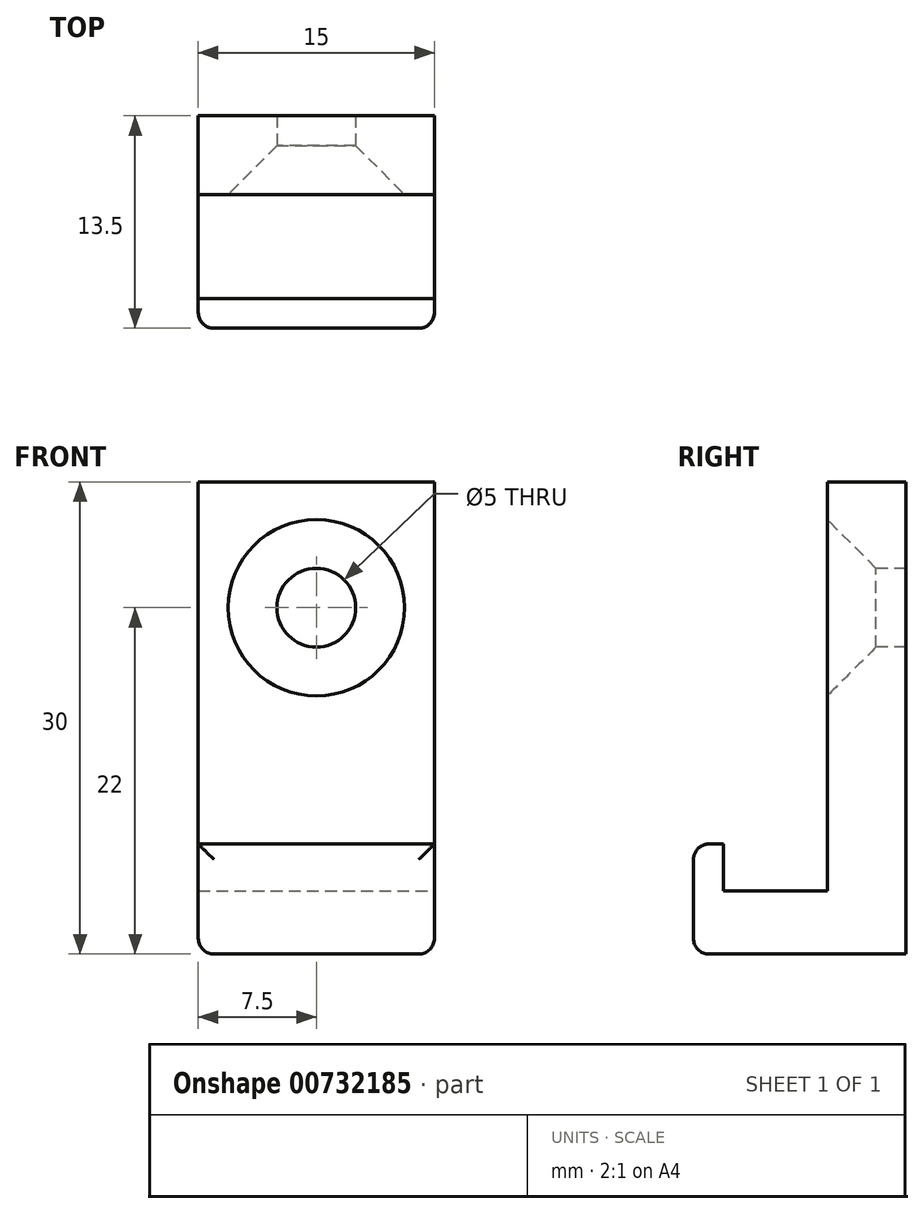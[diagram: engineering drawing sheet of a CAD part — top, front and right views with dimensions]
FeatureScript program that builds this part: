
annotation { "Feature Type Name" : "Feature", "Feature Type Description" : "" }
export const myFeature = defineFeature(function(context is Context, id is Id, definition is map)
    precondition{}
    {
        {
            var Q0;
            Q0=qCreatedBy(makeId("Front.planeOp"),FACE);
            var sketch = newSketch(context, id + "F0", { "sketchPlane" : qUnion([Q0])});
            skLineSegment(sketch, "E0.bottom", {"start": v(-7.5, 15) * mm, "end": v(7.5, 15) * mm});
            skLineSegment(sketch, "E0.top", {"start": v(-7.5, -15) * mm, "end": v(7.5, -15) * mm});
            skLineSegment(sketch, "E0.left", {"start": v(-7.5, 15) * mm, "end": v(-7.5, -15) * mm});
            skLineSegment(sketch, "E0.right", {"start": v(7.5, 15) * mm, "end": v(7.5, -15) * mm});
            skLineSegment(sketch, "E1", {"start": v(-55.38, 0) * mm, "end": v(56.17, 0) * mm, "construction": true});
            skLineSegment(sketch, "E2", {"start": v(0, 15) * mm, "end": v(0, -3.56) * mm, "construction": true});
            skLineSegment(sketch, "E3", {"start": v(-31.34, 0) * mm, "end": v(7.5, 0) * mm, "construction": true});
            skSolve(sketch);
        }
        {
            var Q0;
            Q0=makeQuery(id+"F0.imprint","IMPRINT",FACE,{"disambiguationData":[TD([[makeQuery(id+"F0.imprint","IMPRINT",EDGE,{"derivedFrom":sQuery(id+"F0.wireOp",EDGE,"E0.bottom")}),-1.0]])]});
            extrude(context, id + "F1", {"entities" : qUnion([Q0]), "depth" : 5 * mm, "offsetDistance" : 25 * mm});
        }
        {
            var Q0;
            Q0=makeQuery(id+"F1.opExtrude","CAP_FACE",FACE,{"disambiguationData":[OSD([sQuery(id+"F0.wireOp",EDGE,"E0.bottom"),sQuery(id+"F0.wireOp",EDGE,"E0.top"),sQuery(id+"F0.wireOp",EDGE,"E0.left"),sQuery(id+"F0.wireOp",EDGE,"E0.right")])],"isStart":false});
            var sketch = newSketch(context, id + "F2", { "sketchPlane" : qUnion([Q0])});
            skLineSegment(sketch, "E4", {"start": v(-15.15, 0) * mm, "end": v(12.94, 0) * mm, "construction": true});
            skLineSegment(sketch, "E5", {"start": v(0, -6.11) * mm, "end": v(0, 4.39) * mm, "construction": true});
            skPoint(sketch, "E6", {"position": v(0, 7) * mm});
            skSolve(sketch);
        }
        {
            var Q0;
            Q0=sQuery(id+"F2.wireOp",VERTEX,"E6");
            var Q1;
            Q1=makeQuery(id+"F1.opExtrude","SWEPT_BODY",BODY,{"disambiguationData":[OSD([sQuery(id+"F0.wireOp",EDGE,"E0.bottom"),sQuery(id+"F0.wireOp",EDGE,"E0.top"),sQuery(id+"F0.wireOp",EDGE,"E0.left"),sQuery(id+"F0.wireOp",EDGE,"E0.right")])]});
            hole(context, id + "F3", {"style" : HoleStyle.C_SINK, "endStyle" : HoleEndStyle.THROUGH, "standardTappedOrClearance" : lookupTablePath({ "standard" : "ISO", "size" : "5", "type" : "Drilled" }), "standardBlindInLast" : lookupTablePath({ "standard" : "ISO", "size" : "5", "type" : "Drilled" }), "holeDiameter" : 5 * mm, "cSinkDiameter" : 11.2 * mm, "cSinkAngle" : 90 * degree, "majorDiameter" : 5 * mm, "isTappedThrough" : true, "tappedDepth" : 12 * mm, "tapClearance" : 3, "locations" : qUnion([Q0]), "scope" : qUnion([Q1])});
        }
        {
            var Q0;
            Q0=makeQuery(id+"F1.opExtrude","CAP_FACE",FACE,{"disambiguationData":[OSD([sQuery(id+"F0.wireOp",EDGE,"E0.bottom"),sQuery(id+"F0.wireOp",EDGE,"E0.top"),sQuery(id+"F0.wireOp",EDGE,"E0.left"),sQuery(id+"F0.wireOp",EDGE,"E0.right")])],"isStart":false});
            var sketch = newSketch(context, id + "F4", { "sketchPlane" : qUnion([Q0])});
            skLineSegment(sketch, "E7", {"start": v(-7.5, -11) * mm, "end": v(7.5, -11) * mm});
            skLineSegment(sketch, "E8", {"start": v(7.5, -11) * mm, "end": v(7.5, -15) * mm});
            skLineSegment(sketch, "E9", {"start": v(7.5, -15) * mm, "end": v(-7.5, -15) * mm});
            skLineSegment(sketch, "E10", {"start": v(-7.5, -15) * mm, "end": v(-7.5, -11) * mm});
            skSolve(sketch);
        }
        {
            var Q0;
            Q0=makeQuery(id+"F4.imprint","IMPRINT",FACE,{"disambiguationData":[TD([[makeQuery(id+"F4.imprint","IMPRINT",EDGE,{"derivedFrom":sQuery(id+"F4.wireOp",EDGE,"E7")}),-1.0]])]});
            extrude(context, id + "F5", {"entities" : qUnion([Q0]), "operationType" : NewBodyOperationType.ADD, "depth" : 8.5 * mm, "offsetDistance" : 25 * mm});
        }
        {
            var Q0;
            Q0=makeQuery(id+"F5.opExtrude","SWEPT_FACE",FACE,{"disambiguationData":[OSD([sQuery(id+"F4.wireOp",EDGE,"E7")])]});
            var sketch = newSketch(context, id + "F6", { "sketchPlane" : qUnion([Q0])});
            skLineSegment(sketch, "E11", {"start": v(-7.5, -11.6) * mm, "end": v(7.5, -11.6) * mm});
            skSolve(sketch);
        }
        {
            var Q0;
            {var subQ0=sQuery(id+"F6.wireOp",EDGE,"E11");Q0=makeQuery(id+"F6.imprint","IMPRINT",FACE,{"disambiguationData":[TD([[makeQuery(id+"F6.imprint","IMPRINT",EDGE,{"derivedFrom":subQ0}),-1.0]])]});}
            extrude(context, id + "F7", {"entities" : qUnion([Q0]), "operationType" : NewBodyOperationType.ADD, "depth" : 3 * mm, "offsetDistance" : 25 * mm});
        }
        {
            var Q0;
            Q0=makeQuery(id+"F7.opExtrude","CAP_EDGE",EDGE,{"disambiguationData":[OSD([sQuery(id+"F4.wireOp",EDGE,"E7")])],"isStart":false});
            var Q1;
            {var subQ0=sQuery(id+"F4.wireOp",EDGE,"E8");Q1=makeQuery(id+"F7.boolean.opBoolean","MERGE",EDGE,{"derivedFrom":[makeQuery(id+"F5.opExtrude","CAP_EDGE",EDGE,{"disambiguationData":[OSD([subQ0])],"isStart":false}),makeQuery(id+"F7.opExtrude","SWEPT_EDGE",EDGE,{"disambiguationData":[OSD([sQuery(id+"F0.wireOp",EDGE,"E0.right"),sQuery(id+"F4.wireOp",EDGE,"E7"),subQ0])]})]});}
            var Q2;
            {var subQ0=sQuery(id+"F4.wireOp",EDGE,"E10");Q2=makeQuery(id+"F7.boolean.opBoolean","MERGE",EDGE,{"derivedFrom":[makeQuery(id+"F5.opExtrude","CAP_EDGE",EDGE,{"disambiguationData":[OSD([subQ0])],"isStart":false}),makeQuery(id+"F7.opExtrude","SWEPT_EDGE",EDGE,{"disambiguationData":[OSD([sQuery(id+"F0.wireOp",EDGE,"E0.left"),sQuery(id+"F4.wireOp",EDGE,"E7"),subQ0])]})]});}
            var Q3;
            Q3=makeQuery(id+"F5.opExtrude","CAP_EDGE",EDGE,{"disambiguationData":[OSD([sQuery(id+"F4.wireOp",EDGE,"E9")])],"isStart":false});
            var Q4;
            Q4=makeQuery(id+"F5.boolean.opBoolean","MERGE",EDGE,{"derivedFrom":[makeQuery(id+"F1.opExtrude","SWEPT_EDGE",EDGE,{"disambiguationData":[OSD([sQuery(id+"F0.wireOp",EDGE,"E0.top"),sQuery(id+"F0.wireOp",EDGE,"E0.right")])]}),makeQuery(id+"F5.opExtrude","SWEPT_EDGE",EDGE,{"disambiguationData":[OSD([sQuery(id+"F4.wireOp",EDGE,"E8"),sQuery(id+"F4.wireOp",EDGE,"E9")])]})]});
            var Q5;
            Q5=makeQuery(id+"F5.boolean.opBoolean","MERGE",EDGE,{"derivedFrom":[makeQuery(id+"F1.opExtrude","SWEPT_EDGE",EDGE,{"disambiguationData":[OSD([sQuery(id+"F0.wireOp",EDGE,"E0.top"),sQuery(id+"F0.wireOp",EDGE,"E0.left")])]}),makeQuery(id+"F5.opExtrude","SWEPT_EDGE",EDGE,{"disambiguationData":[OSD([sQuery(id+"F4.wireOp",EDGE,"E9"),sQuery(id+"F4.wireOp",EDGE,"E10")])]})]});
            fillet(context, id + "F8", {"entities" : qUnion([Q0, Q1, Q2, Q3, Q4, Q5]), "radius" : 1 * mm, "tangentPropagation" : true, "allowEdgeOverflow" : false});
        }
    });
